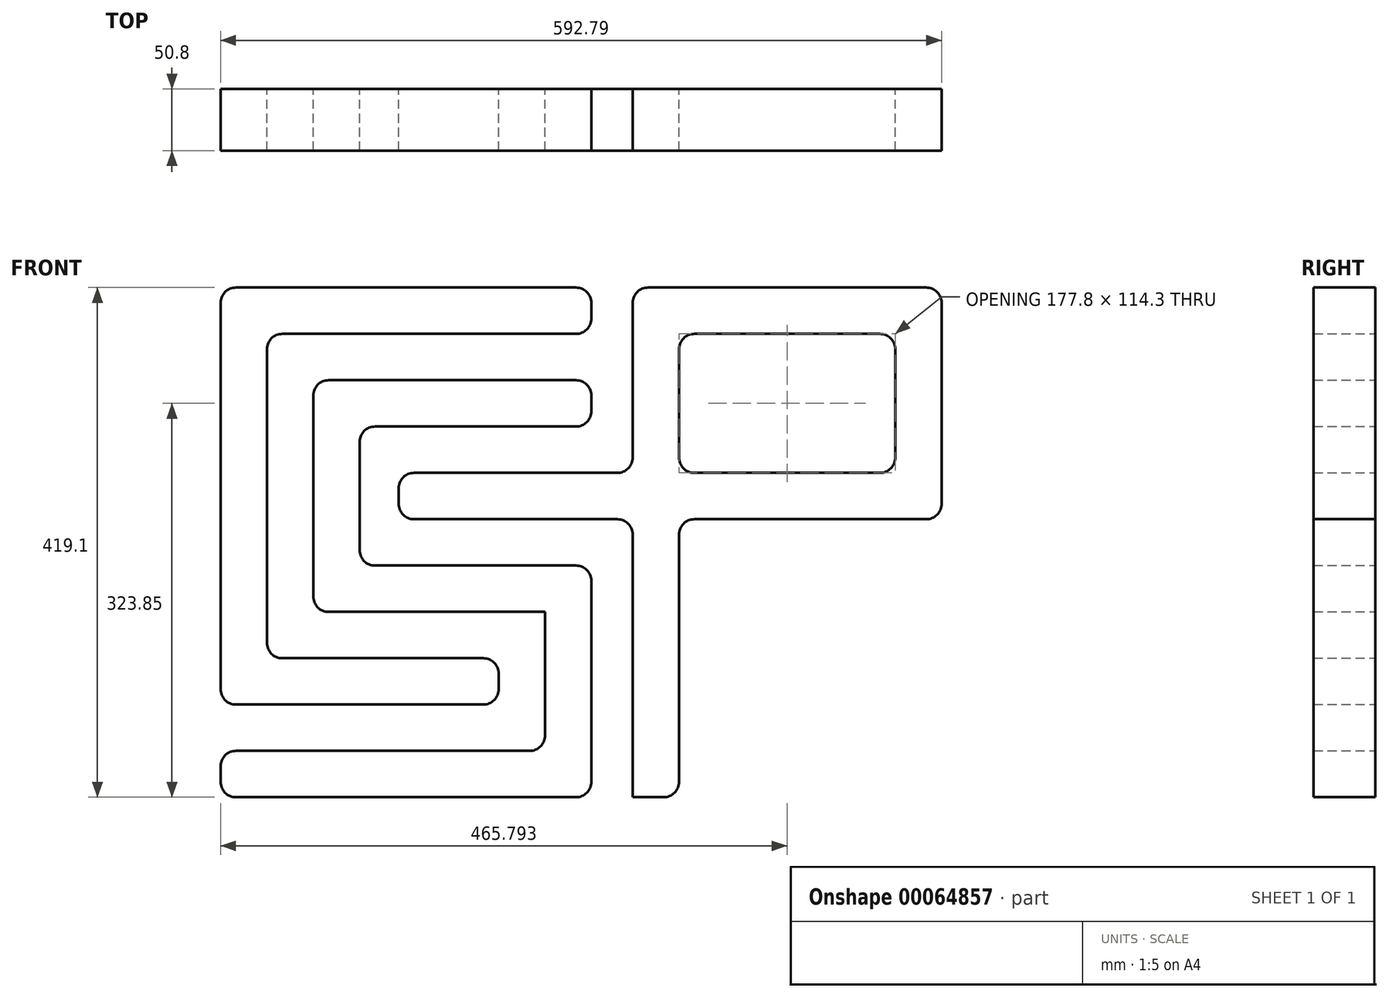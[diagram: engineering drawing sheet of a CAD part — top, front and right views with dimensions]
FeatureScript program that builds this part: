
annotation { "Feature Type Name" : "Feature", "Feature Type Description" : "" }
export const myFeature = defineFeature(function(context is Context, id is Id, definition is map)
    precondition{}
    {
        {
            var Q0;
            Q0=qCreatedBy(makeId("Front.planeOp"),FACE);
            var sketch = newSketch(context, id + "F0", { "sketchPlane" : qUnion([Q0])});
            skLineSegment(sketch, "E0", {"start": v(-304.8, 0) * mm, "end": v(-304.8, 342.9) * mm});
            skLineSegment(sketch, "E1", {"start": v(-304.8, 342.9) * mm, "end": v(0, 342.9) * mm});
            skLineSegment(sketch, "E2", {"start": v(0, 342.9) * mm, "end": v(0, 304.8) * mm});
            skLineSegment(sketch, "E3", {"start": v(0, 304.8) * mm, "end": v(-266.7, 304.8) * mm});
            skLineSegment(sketch, "E4", {"start": v(-266.7, 304.8) * mm, "end": v(-266.7, 38.1) * mm});
            skLineSegment(sketch, "E5", {"start": v(0, 266.7) * mm, "end": v(-228.6, 266.7) * mm});
            skLineSegment(sketch, "E6", {"start": v(-266.7, 38.1) * mm, "end": v(-76.2, 38.1) * mm});
            skLineSegment(sketch, "E7", {"start": v(-76.2, 38.1) * mm, "end": v(-76.2, 0) * mm});
            skLineSegment(sketch, "E8", {"start": v(-76.2, 0) * mm, "end": v(-304.8, 0) * mm});
            skLineSegment(sketch, "E9", {"start": v(-228.6, 266.7) * mm, "end": v(-228.6, 76.2) * mm});
            skLineSegment(sketch, "E10", {"start": v(-228.6, 76.2) * mm, "end": v(-38.1, 76.2) * mm});
            skLineSegment(sketch, "E11", {"start": v(-38.1, 76.2) * mm, "end": v(-38.1, -38.1) * mm});
            skLineSegment(sketch, "E12", {"start": v(0, -76.2) * mm, "end": v(0, 114.3) * mm});
            skLineSegment(sketch, "E13", {"start": v(0, 114.3) * mm, "end": v(-190.5, 114.3) * mm});
            skLineSegment(sketch, "E14", {"start": v(-190.5, 114.3) * mm, "end": v(-190.5, 228.6) * mm});
            skLineSegment(sketch, "E15", {"start": v(-190.5, 228.6) * mm, "end": v(0, 228.6) * mm});
            skLineSegment(sketch, "E16", {"start": v(0, 228.6) * mm, "end": v(0, 266.7) * mm});
            skLineSegment(sketch, "E17", {"start": v(-38.1, -38.1) * mm, "end": v(-304.8, -38.1) * mm});
            skLineSegment(sketch, "E18", {"start": v(-304.8, -38.1) * mm, "end": v(-304.8, -76.2) * mm});
            skLineSegment(sketch, "E19", {"start": v(-304.8, -76.2) * mm, "end": v(0, -76.2) * mm});
            skLineSegment(sketch, "E20", {"start": v(-158.37, 190.5) * mm, "end": v(-158.37, 152.4) * mm});
            skLineSegment(sketch, "E21", {"start": v(-158.37, 152.4) * mm, "end": v(34, 152.4) * mm});
            skLineSegment(sketch, "E22", {"start": v(34, 152.4) * mm, "end": v(34, -76.2) * mm});
            skLineSegment(sketch, "E23", {"start": v(34, -76.2) * mm, "end": v(72.1, -76.2) * mm});
            skLineSegment(sketch, "E24", {"start": v(72.1, -76.2) * mm, "end": v(72.1, 152.4) * mm});
            skLineSegment(sketch, "E25", {"start": v(72.1, 152.4) * mm, "end": v(288, 152.4) * mm});
            skLineSegment(sketch, "E26", {"start": v(288, 152.4) * mm, "end": v(288, 342.9) * mm});
            skLineSegment(sketch, "E27", {"start": v(288, 342.9) * mm, "end": v(34, 342.9) * mm});
            skLineSegment(sketch, "E28", {"start": v(34, 342.9) * mm, "end": v(34, 190.5) * mm});
            skLineSegment(sketch, "E29", {"start": v(34, 190.5) * mm, "end": v(-158.37, 190.5) * mm});
            skLineSegment(sketch, "E30.bottom", {"start": v(72.1, 190.5) * mm, "end": v(249.9, 190.5) * mm});
            skLineSegment(sketch, "E30.top", {"start": v(72.1, 304.8) * mm, "end": v(249.9, 304.8) * mm});
            skLineSegment(sketch, "E30.left", {"start": v(72.1, 190.5) * mm, "end": v(72.1, 304.8) * mm});
            skLineSegment(sketch, "E30.right", {"start": v(249.9, 190.5) * mm, "end": v(249.9, 304.8) * mm});
            skSolve(sketch);
        }
        {
            var Q0;
            Q0=makeQuery(id+"F0.imprint","IMPRINT",FACE,{"disambiguationData":[TD([[makeQuery(id+"F0.imprint","IMPRINT",EDGE,{"derivedFrom":sQuery(id+"F0.wireOp",EDGE,"E0")}),-1.0]])]});
            var Q1;
            Q1=makeQuery(id+"F0.imprint","IMPRINT",FACE,{"disambiguationData":[TD([[makeQuery(id+"F0.imprint","IMPRINT",EDGE,{"derivedFrom":sQuery(id+"F0.wireOp",EDGE,"E5")}),1.0]])]});
            var Q2;
            Q2=makeQuery(id+"F0.imprint","IMPRINT",FACE,{"disambiguationData":[TD([[makeQuery(id+"F0.imprint","IMPRINT",EDGE,{"derivedFrom":sQuery(id+"F0.wireOp",EDGE,"E20")}),1.0]])]});
            extrude(context, id + "F1", {"entities" : qUnion([Q0, Q1, Q2]), "depth" : 50.8 * mm});
        }
        {
            var Q0;
            Q0=makeQuery(id+"F1.opExtrude","SWEPT_EDGE",EDGE,{"disambiguationData":[OSD([sQuery(id+"F0.wireOp",EDGE,"E26"),sQuery(id+"F0.wireOp",EDGE,"E27")])]});
            var Q1;
            Q1=makeQuery(id+"F1.opExtrude","SWEPT_EDGE",EDGE,{"disambiguationData":[OSD([sQuery(id+"F0.wireOp",EDGE,"E25"),sQuery(id+"F0.wireOp",EDGE,"E26")])]});
            var Q2;
            Q2=makeQuery(id+"F1.opExtrude","SWEPT_EDGE",EDGE,{"disambiguationData":[OSD([sQuery(id+"F0.wireOp",EDGE,"E27"),sQuery(id+"F0.wireOp",EDGE,"E28")])]});
            var Q3;
            Q3=makeQuery(id+"F1.opExtrude","SWEPT_EDGE",EDGE,{"disambiguationData":[OSD([sQuery(id+"F0.wireOp",EDGE,"E1"),sQuery(id+"F0.wireOp",EDGE,"E2")])]});
            var Q4;
            Q4=makeQuery(id+"F1.opExtrude","SWEPT_EDGE",EDGE,{"disambiguationData":[OSD([sQuery(id+"F0.wireOp",EDGE,"E2"),sQuery(id+"F0.wireOp",EDGE,"E3")])]});
            var Q5;
            Q5=makeQuery(id+"F1.opExtrude","SWEPT_EDGE",EDGE,{"disambiguationData":[OSD([sQuery(id+"F0.wireOp",EDGE,"E5"),sQuery(id+"F0.wireOp",EDGE,"E16")])]});
            var Q6;
            Q6=makeQuery(id+"F1.opExtrude","SWEPT_EDGE",EDGE,{"disambiguationData":[OSD([sQuery(id+"F0.wireOp",EDGE,"E15"),sQuery(id+"F0.wireOp",EDGE,"E16")])]});
            var Q7;
            Q7=makeQuery(id+"F1.opExtrude","SWEPT_EDGE",EDGE,{"disambiguationData":[OSD([sQuery(id+"F0.wireOp",EDGE,"E20"),sQuery(id+"F0.wireOp",EDGE,"E29")])]});
            var Q8;
            Q8=makeQuery(id+"F1.opExtrude","SWEPT_EDGE",EDGE,{"disambiguationData":[OSD([sQuery(id+"F0.wireOp",EDGE,"E5"),sQuery(id+"F0.wireOp",EDGE,"E9")])]});
            var Q9;
            Q9=makeQuery(id+"F1.opExtrude","SWEPT_EDGE",EDGE,{"disambiguationData":[OSD([sQuery(id+"F0.wireOp",EDGE,"E0"),sQuery(id+"F0.wireOp",EDGE,"E1")])]});
            var Q10;
            Q10=makeQuery(id+"F1.opExtrude","SWEPT_EDGE",EDGE,{"disambiguationData":[OSD([sQuery(id+"F0.wireOp",EDGE,"E17"),sQuery(id+"F0.wireOp",EDGE,"E18")])]});
            var Q11;
            Q11=makeQuery(id+"F1.opExtrude","SWEPT_EDGE",EDGE,{"disambiguationData":[OSD([sQuery(id+"F0.wireOp",EDGE,"E12"),sQuery(id+"F0.wireOp",EDGE,"E13")])]});
            var Q12;
            Q12=makeQuery(id+"F1.opExtrude","SWEPT_EDGE",EDGE,{"disambiguationData":[OSD([sQuery(id+"F0.wireOp",EDGE,"E23"),sQuery(id+"F0.wireOp",EDGE,"E24")])]});
            var Q13;
            Q13=makeQuery(id+"F1.opExtrude","SWEPT_EDGE",EDGE,{"disambiguationData":[OSD([sQuery(id+"F0.wireOp",EDGE,"E12"),sQuery(id+"F0.wireOp",EDGE,"E19")])]});
            var Q14;
            Q14=makeQuery(id+"F1.opExtrude","SWEPT_EDGE",EDGE,{"disambiguationData":[OSD([sQuery(id+"F0.wireOp",EDGE,"E13"),sQuery(id+"F0.wireOp",EDGE,"E14")])]});
            var Q15;
            Q15=makeQuery(id+"F1.opExtrude","SWEPT_EDGE",EDGE,{"disambiguationData":[OSD([sQuery(id+"F0.wireOp",EDGE,"E4"),sQuery(id+"F0.wireOp",EDGE,"E6")])]});
            var Q16;
            Q16=makeQuery(id+"F1.opExtrude","SWEPT_EDGE",EDGE,{"disambiguationData":[OSD([sQuery(id+"F0.wireOp",EDGE,"E3"),sQuery(id+"F0.wireOp",EDGE,"E4")])]});
            var Q17;
            Q17=makeQuery(id+"F1.opExtrude","SWEPT_EDGE",EDGE,{"disambiguationData":[OSD([sQuery(id+"F0.wireOp",EDGE,"E14"),sQuery(id+"F0.wireOp",EDGE,"E15")])]});
            var Q18;
            Q18=makeQuery(id+"F1.opExtrude","SWEPT_EDGE",EDGE,{"disambiguationData":[OSD([sQuery(id+"F0.wireOp",EDGE,"E20"),sQuery(id+"F0.wireOp",EDGE,"E21")])]});
            var Q19;
            Q19=makeQuery(id+"F1.opExtrude","SWEPT_EDGE",EDGE,{"disambiguationData":[OSD([sQuery(id+"F0.wireOp",EDGE,"E30.top"),sQuery(id+"F0.wireOp",EDGE,"E30.left")])]});
            var Q20;
            Q20=makeQuery(id+"F1.opExtrude","SWEPT_EDGE",EDGE,{"disambiguationData":[OSD([sQuery(id+"F0.wireOp",EDGE,"E24"),sQuery(id+"F0.wireOp",EDGE,"E25")])]});
            var Q21;
            Q21=makeQuery(id+"F1.opExtrude","SWEPT_EDGE",EDGE,{"disambiguationData":[OSD([sQuery(id+"F0.wireOp",EDGE,"E30.bottom"),sQuery(id+"F0.wireOp",EDGE,"E30.left")])]});
            var Q22;
            Q22=makeQuery(id+"F1.opExtrude","SWEPT_EDGE",EDGE,{"disambiguationData":[OSD([sQuery(id+"F0.wireOp",EDGE,"E18"),sQuery(id+"F0.wireOp",EDGE,"E19")])]});
            var Q23;
            Q23=makeQuery(id+"F1.opExtrude","SWEPT_EDGE",EDGE,{"disambiguationData":[OSD([sQuery(id+"F0.wireOp",EDGE,"E0"),sQuery(id+"F0.wireOp",EDGE,"E8")])]});
            var Q24;
            Q24=makeQuery(id+"F1.opExtrude","SWEPT_EDGE",EDGE,{"disambiguationData":[OSD([sQuery(id+"F0.wireOp",EDGE,"E9"),sQuery(id+"F0.wireOp",EDGE,"E10")])]});
            var Q25;
            Q25=makeQuery(id+"F1.opExtrude","SWEPT_EDGE",EDGE,{"disambiguationData":[OSD([sQuery(id+"F0.wireOp",EDGE,"E28"),sQuery(id+"F0.wireOp",EDGE,"E29")])]});
            var Q26;
            Q26=makeQuery(id+"F1.opExtrude","SWEPT_EDGE",EDGE,{"disambiguationData":[OSD([sQuery(id+"F0.wireOp",EDGE,"E21"),sQuery(id+"F0.wireOp",EDGE,"E22")])]});
            var Q27;
            Q27=makeQuery(id+"F1.opExtrude","SWEPT_EDGE",EDGE,{"disambiguationData":[OSD([sQuery(id+"F0.wireOp",EDGE,"E30.bottom"),sQuery(id+"F0.wireOp",EDGE,"E30.right")])]});
            var Q28;
            Q28=makeQuery(id+"F1.opExtrude","SWEPT_EDGE",EDGE,{"disambiguationData":[OSD([sQuery(id+"F0.wireOp",EDGE,"E30.top"),sQuery(id+"F0.wireOp",EDGE,"E30.right")])]});
            var Q29;
            Q29=makeQuery(id+"F1.opExtrude","SWEPT_EDGE",EDGE,{"disambiguationData":[OSD([sQuery(id+"F0.wireOp",EDGE,"E6"),sQuery(id+"F0.wireOp",EDGE,"E7")])]});
            var Q30;
            Q30=makeQuery(id+"F1.opExtrude","SWEPT_EDGE",EDGE,{"disambiguationData":[OSD([sQuery(id+"F0.wireOp",EDGE,"E11"),sQuery(id+"F0.wireOp",EDGE,"E17")])]});
            var Q31;
            Q31=makeQuery(id+"F1.opExtrude","SWEPT_EDGE",EDGE,{"disambiguationData":[OSD([sQuery(id+"F0.wireOp",EDGE,"E7"),sQuery(id+"F0.wireOp",EDGE,"E8")])]});
            fillet(context, id + "F2", {"entities" : qUnion([Q0, Q1, Q2, Q3, Q4, Q5, Q6, Q7, Q8, Q9, Q10, Q11, Q12, Q13, Q14, Q15, Q16, Q17, Q18, Q19, Q20, Q21, Q22, Q23, Q24, Q25, Q26, Q27, Q28, Q29, Q30, Q31]), "radius" : 12.7 * mm, "tangentPropagation" : true, "allowEdgeOverflow" : false});
        }
    });
